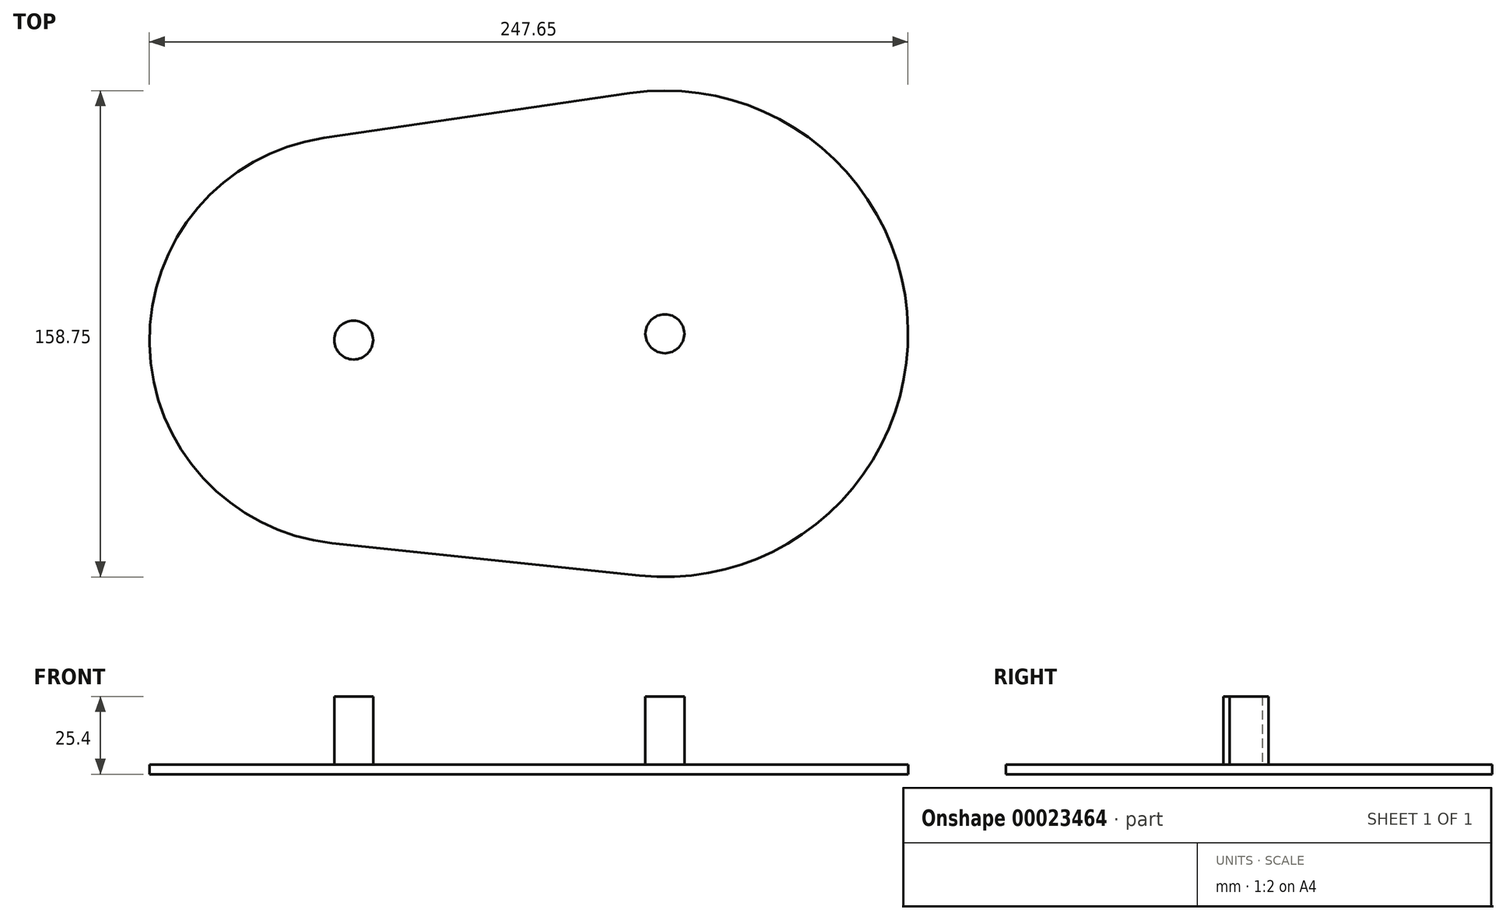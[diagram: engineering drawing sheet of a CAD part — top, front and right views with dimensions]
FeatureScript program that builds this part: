
annotation { "Feature Type Name" : "Feature", "Feature Type Description" : "" }
export const myFeature = defineFeature(function(context is Context, id is Id, definition is map)
    precondition{}
    {
        {
            var Q0;
            Q0=qCreatedBy(makeId("Top.planeOp"),FACE);
            var sketch = newSketch(context, id + "F0", { "sketchPlane" : qUnion([Q0])});
            skPoint(sketch, "E0.rect.middle", {"position": v(0, 0) * mm});
            skArc(sketch, "E1", {"start": v(53.62, -77.91) * mm, "mid": v(141.32, 2.62) * mm, "end": v(50.46, 79.56) * mm});
            skCircle(sketch, "E2", {"center": v(-39.64, -1.02) * mm, "radius": 6.35 * mm});
            skCircle(sketch, "E3", {"center": v(61.96, 1.02) * mm, "radius": 6.35 * mm});
            skLineSegment(sketch, "E4", {"start": v(-49.3, 64.95) * mm, "end": v(50.46, 79.56) * mm});
            skLineSegment(sketch, "E5", {"start": v(53.62, -77.91) * mm, "end": v(-46.64, -67.33) * mm});
            skArc(sketch, "E6", {"start": v(-49.3, 64.95) * mm, "mid": v(-106.3, -2.36) * mm, "end": v(-46.64, -67.33) * mm});
            skSolve(sketch);
        }
        {
            var Q0;
            {var subQ0=sQuery(id+"F0.wireOp",EDGE,"E2");var subQ1=sQuery(id+"F0.wireOp",EDGE,"E0.rect.right");var subQ3=makeQuery(id+"F0.imprint","INTERSECT",VERTEX,{"disambiguationData":[OD(0.0)],"derivedFrom":[subQ1,subQ0]});Q0=makeQuery(id+"F0.imprint","IMPRINT",FACE,{"disambiguationData":[TD([[makeQuery(id+"F0.imprint","IMPRINT",EDGE,{"disambiguationData":[TD([[subQ3,-1.0]])],"derivedFrom":subQ0}),-1.0]])]});}
            var Q1;
            {var subQ0=sQuery(id+"F0.wireOp",EDGE,"E2");var subQ1=sQuery(id+"F0.wireOp",EDGE,"E0.rect.right");var subQ3=makeQuery(id+"F0.imprint","INTERSECT",VERTEX,{"disambiguationData":[OD(0.0)],"derivedFrom":[subQ1,subQ0]});Q1=makeQuery(id+"F0.imprint","IMPRINT",FACE,{"disambiguationData":[TD([[makeQuery(id+"F0.imprint","IMPRINT",EDGE,{"disambiguationData":[TD([[subQ3,1.0]])],"derivedFrom":subQ0}),-1.0]])]});}
            var Q2;
            {var subQ3=sQuery(id+"F0.wireOp",EDGE,"E0.rect.bottom");Q2=makeQuery(id+"F0.imprint","IMPRINT",FACE,{"disambiguationData":[TD([[makeQuery(id+"F0.imprint","IMPRINT",EDGE,{"derivedFrom":subQ3}),1.0]])]});}
            var Q3;
            {var subQ0=sQuery(id+"F0.wireOp",EDGE,"E3");var subQ1=sQuery(id+"F0.wireOp",EDGE,"E0.rect.left");var subQ3=makeQuery(id+"F0.imprint","INTERSECT",VERTEX,{"disambiguationData":[OD(0.0)],"derivedFrom":[subQ1,subQ0]});Q3=makeQuery(id+"F0.imprint","IMPRINT",FACE,{"disambiguationData":[TD([[makeQuery(id+"F0.imprint","IMPRINT",EDGE,{"disambiguationData":[TD([[subQ3,-1.0]])],"derivedFrom":subQ0}),-1.0]])]});}
            var Q4;
            {var subQ0=sQuery(id+"F0.wireOp",EDGE,"E3");var subQ1=sQuery(id+"F0.wireOp",EDGE,"E0.rect.left");var subQ3=makeQuery(id+"F0.imprint","INTERSECT",VERTEX,{"disambiguationData":[OD(0.0)],"derivedFrom":[subQ1,subQ0]});Q4=makeQuery(id+"F0.imprint","IMPRINT",FACE,{"disambiguationData":[TD([[makeQuery(id+"F0.imprint","IMPRINT",EDGE,{"disambiguationData":[TD([[subQ3,1.0]])],"derivedFrom":subQ0}),-1.0]])]});}
            var Q5;
            {var subQ0=sQuery(id+"F0.wireOp",EDGE,"E1");var subQ1=sQuery(id+"F0.wireOp",EDGE,"444f68a8-5412-4927-ad56-f04459f07ddd");var subQ3=makeQuery(id+"F0.imprint","INTERSECT",VERTEX,{"disambiguationData":[OD(0.0)],"derivedFrom":[subQ1,subQ0]});Q5=makeQuery(id+"F0.imprint","IMPRINT",FACE,{"disambiguationData":[TD([[makeQuery(id+"F0.imprint","IMPRINT",EDGE,{"disambiguationData":[TD([[subQ3,1.0]])],"derivedFrom":subQ1}),1.0]])]});}
            var Q6;
            {var subQ3=sQuery(id+"F0.wireOp",EDGE,"E0.rect.top");Q6=makeQuery(id+"F0.imprint","IMPRINT",FACE,{"disambiguationData":[TD([[makeQuery(id+"F0.imprint","IMPRINT",EDGE,{"derivedFrom":subQ3}),-1.0]])]});}
            var Q7;
            Q7=makeQuery(id+"F0.imprint","IMPRINT",FACE,{"disambiguationData":[TD([[makeQuery(id+"F0.imprint","IMPRINT",EDGE,{"derivedFrom":sQuery(id+"F0.wireOp",EDGE,"E1")}),1.0]])]});
            extrude(context, id + "F1", {"entities" : qUnion([Q0, Q1, Q2, Q3, Q4, Q5, Q6, Q7]), "depth" : 3.17 * mm});
        }
        {
            var Q0;
            {var subQ0=sQuery(id+"F0.wireOp",EDGE,"E3");var subQ1=sQuery(id+"F0.wireOp",EDGE,"E0.rect.left");var subQ3=makeQuery(id+"F0.imprint","INTERSECT",VERTEX,{"disambiguationData":[OD(0.0)],"derivedFrom":[subQ1,subQ0]});Q0=makeQuery(id+"F0.imprint","IMPRINT",FACE,{"disambiguationData":[TD([[makeQuery(id+"F0.imprint","IMPRINT",EDGE,{"disambiguationData":[TD([[subQ3,-1.0]])],"derivedFrom":subQ1}),1.0]])]});}
            var Q1;
            {var subQ0=sQuery(id+"F0.wireOp",EDGE,"E3");var subQ1=sQuery(id+"F0.wireOp",EDGE,"E0.rect.left");var subQ3=makeQuery(id+"F0.imprint","INTERSECT",VERTEX,{"disambiguationData":[OD(0.0)],"derivedFrom":[subQ1,subQ0]});Q1=makeQuery(id+"F0.imprint","IMPRINT",FACE,{"disambiguationData":[TD([[makeQuery(id+"F0.imprint","IMPRINT",EDGE,{"disambiguationData":[TD([[subQ3,-1.0]])],"derivedFrom":subQ1}),-1.0]])]});}
            var Q2;
            {var subQ0=sQuery(id+"F0.wireOp",EDGE,"E2");var subQ1=sQuery(id+"F0.wireOp",EDGE,"E0.rect.right");var subQ3=makeQuery(id+"F0.imprint","INTERSECT",VERTEX,{"disambiguationData":[OD(0.0)],"derivedFrom":[subQ1,subQ0]});Q2=makeQuery(id+"F0.imprint","IMPRINT",FACE,{"disambiguationData":[TD([[makeQuery(id+"F0.imprint","IMPRINT",EDGE,{"disambiguationData":[TD([[subQ3,-1.0]])],"derivedFrom":subQ1}),-1.0]])]});}
            var Q3;
            {var subQ0=sQuery(id+"F0.wireOp",EDGE,"E2");var subQ1=sQuery(id+"F0.wireOp",EDGE,"E0.rect.right");var subQ3=makeQuery(id+"F0.imprint","INTERSECT",VERTEX,{"disambiguationData":[OD(0.0)],"derivedFrom":[subQ1,subQ0]});Q3=makeQuery(id+"F0.imprint","IMPRINT",FACE,{"disambiguationData":[TD([[makeQuery(id+"F0.imprint","IMPRINT",EDGE,{"disambiguationData":[TD([[subQ3,-1.0]])],"derivedFrom":subQ1}),1.0]])]});}
            var Q4;
            Q4=makeQuery(id+"F0.imprint","IMPRINT",FACE,{"disambiguationData":[TD([[makeQuery(id+"F0.imprint","IMPRINT",EDGE,{"derivedFrom":sQuery(id+"F0.wireOp",EDGE,"E2")}),1.0]])]});
            var Q5;
            Q5=makeQuery(id+"F0.imprint","IMPRINT",FACE,{"disambiguationData":[TD([[makeQuery(id+"F0.imprint","IMPRINT",EDGE,{"derivedFrom":sQuery(id+"F0.wireOp",EDGE,"E3")}),1.0]])]});
            extrude(context, id + "F2", {"entities" : qUnion([Q0, Q1, Q2, Q3, Q4, Q5]), "operationType" : NewBodyOperationType.ADD, "depth" : 25.4 * mm});
        }
    });
